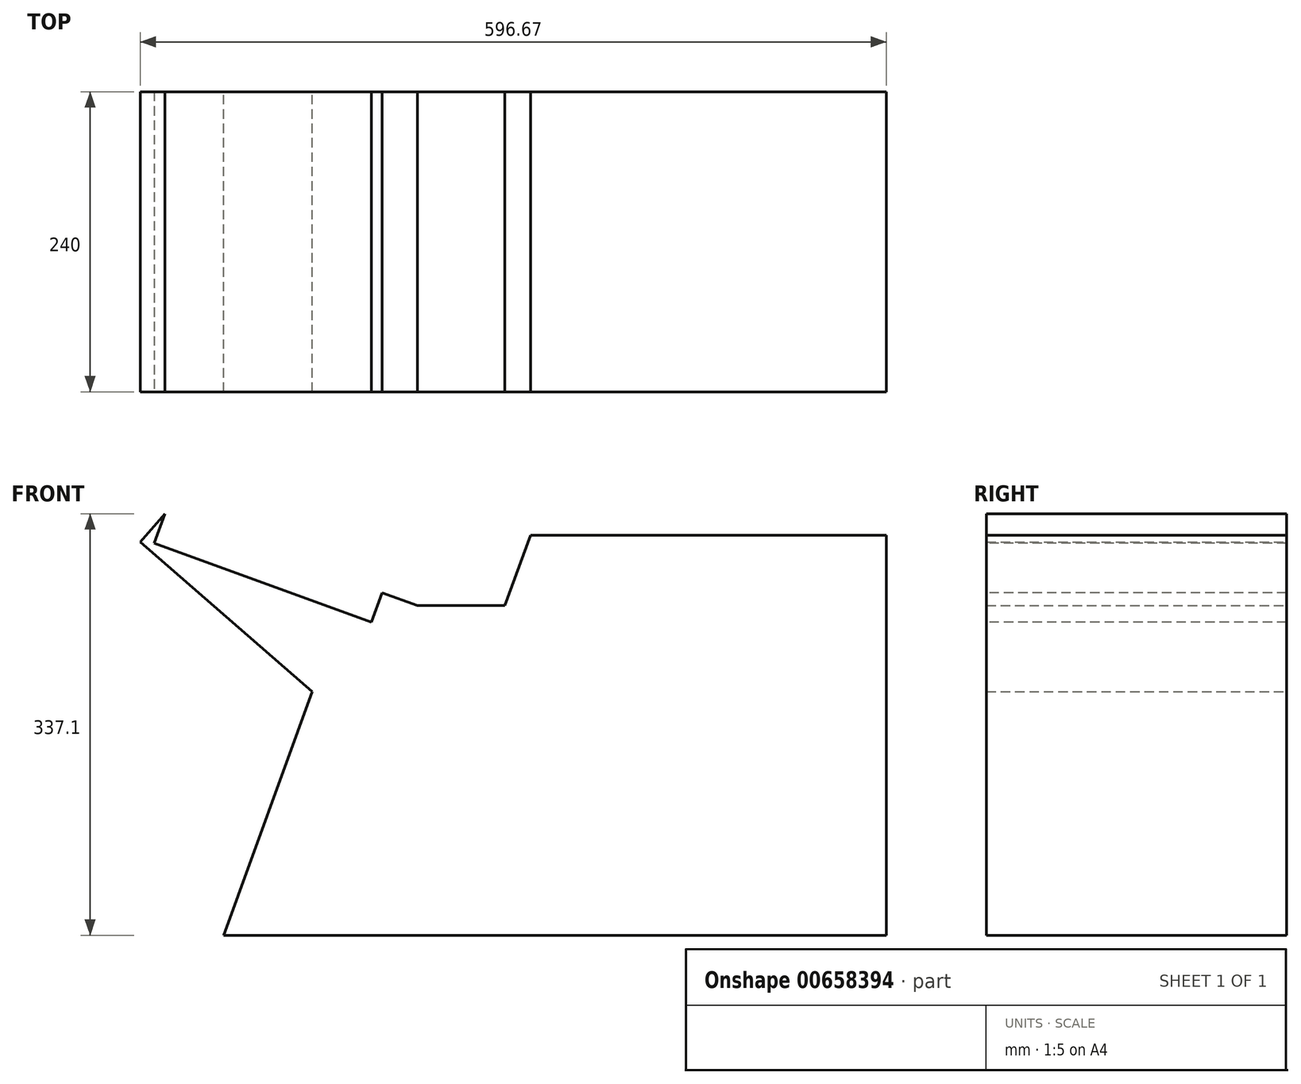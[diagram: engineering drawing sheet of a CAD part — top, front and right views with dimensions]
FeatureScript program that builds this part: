
annotation { "Feature Type Name" : "Feature", "Feature Type Description" : "" }
export const myFeature = defineFeature(function(context is Context, id is Id, definition is map)
    precondition{}
    {
        {
            var Q0;
            Q0=qCreatedBy(makeId("Front.planeOp"),FACE);
            var sketch = newSketch(context, id + "F0", { "sketchPlane" : qUnion([Q0])});
            skLineSegment(sketch, "E0.bottom", {"start": v(265, 160) * mm, "end": v(-265, 160) * mm});
            skLineSegment(sketch, "E0.top", {"start": v(265, -160) * mm, "end": v(-265, -160) * mm});
            skLineSegment(sketch, "E0.left", {"start": v(265, 160) * mm, "end": v(265, -160) * mm});
            skLineSegment(sketch, "E0.right", {"start": v(-265, 160) * mm, "end": v(-265, -160) * mm});
            skPoint(sketch, "E0.middle", {"position": v(0, 0) * mm});
            skLineSegment(sketch, "E1", {"start": v(-265, -160) * mm, "end": v(-194.1, 34.8) * mm});
            skLineSegment(sketch, "E2", {"start": v(-194.1, 34.8) * mm, "end": v(-331.67, 154.47) * mm});
            skLineSegment(sketch, "E3", {"start": v(-331.67, 154.47) * mm, "end": v(-311.98, 177.1) * mm});
            skLineSegment(sketch, "E4", {"start": v(-311.98, 177.1) * mm, "end": v(-265, 160) * mm});
            skLineSegment(sketch, "E5", {"start": v(-311.98, 177.1) * mm, "end": v(-109.95, 103.57) * mm});
            skLineSegment(sketch, "E6", {"start": v(-109.95, 103.57) * mm, "end": v(-39.95, 103.57) * mm});
            skLineSegment(sketch, "E7", {"start": v(-39.95, 103.57) * mm, "end": v(-19.41, 160) * mm});
            skLineSegment(sketch, "E8", {"start": v(0, 160) * mm, "end": v(265, 160) * mm});
            skSolve(sketch);
        }
        {
            var Q0;
            {var subQ5=sQuery(id+"F0.wireOp",EDGE,"E3");Q0=makeQuery(id+"F0.imprint","IMPRINT",FACE,{"disambiguationData":[TD([[makeQuery(id+"F0.imprint","IMPRINT",EDGE,{"derivedFrom":subQ5}),-1.0]])]});}
            var Q1;
            Q1=makeQuery(id+"F0.imprint","IMPRINT",FACE,{"disambiguationData":[TD([[makeQuery(id+"F0.imprint","IMPRINT",EDGE,{"derivedFrom":sQuery(id+"F0.wireOp",EDGE,"E0.top")}),-1.0]])]});
            extrude(context, id + "F1", {"entities" : qUnion([Q0, Q1]), "depth" : 240 * mm, "offsetDistance" : 25 * mm});
        }
        {
            var Q0;
            Q0=makeQuery(id+"F1.opExtrude","CAP_FACE",FACE,{"disambiguationData":[OSD([sQuery(id+"F0.wireOp",EDGE,"E0.bottom"),sQuery(id+"F0.wireOp",EDGE,"E0.top"),sQuery(id+"F0.wireOp",EDGE,"E0.left"),sQuery(id+"F0.wireOp",EDGE,"E1"),sQuery(id+"F0.wireOp",EDGE,"E2"),sQuery(id+"F0.wireOp",EDGE,"E3"),sQuery(id+"F0.wireOp",EDGE,"E5"),sQuery(id+"F0.wireOp",EDGE,"E6"),sQuery(id+"F0.wireOp",EDGE,"E7"),sQuery(id+"F0.wireOp",EDGE,"E8")])],"isStart":false});
            var sketch = newSketch(context, id + "F2", { "sketchPlane" : qUnion([Q0])});
            skLineSegment(sketch, "E9", {"start": v(-311.98, 177.1) * mm, "end": v(-320.54, 153.6) * mm});
            skLineSegment(sketch, "E10", {"start": v(-320.54, 153.6) * mm, "end": v(-146.7, 90.33) * mm});
            skLineSegment(sketch, "E11", {"start": v(-146.7, 90.33) * mm, "end": v(-138.14, 113.83) * mm});
            skLineSegment(sketch, "E12", {"start": v(-138.14, 113.83) * mm, "end": v(-311.98, 177.1) * mm});
            skSolve(sketch);
        }
        {
            var Q0;
            Q0=makeQuery(id+"F2.imprint","IMPRINT",FACE,{"disambiguationData":[TD([[makeQuery(id+"F2.imprint","IMPRINT",EDGE,{"derivedFrom":sQuery(id+"F2.wireOp",EDGE,"E9")}),1.0]])]});
            extrude(context, id + "F3", {"entities" : qUnion([Q0]), "operationType" : NewBodyOperationType.REMOVE, "oppositeDirection" : true, "depth" : 240 * mm, "offsetDistance" : 25 * mm});
        }
    });
